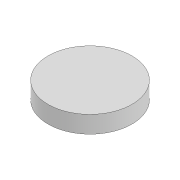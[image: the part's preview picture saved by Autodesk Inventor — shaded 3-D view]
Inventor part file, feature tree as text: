
AUTODESK INVENTOR PART (.ipt)
format: ipt  version: 2020.3 (Build 243373000, 373)  size: 73,728 bytes
history: native  units: mm
features: extrude x1, sketch x1
ambient origin geometry x8: Origin, YZ Plane, XZ Plane, XY Plane, X Axis, Y Axis, Z Axis, Center Point
bodies: Solid1 (feature_tree)
feature tree (2):
  extrude  "Extrusion1"  Depth=5.0mm TaperAngle=0.0deg
  sketch  "Sketch1"  dims[d0=24.5mm d1=5.0mm d2=0.0mm]
